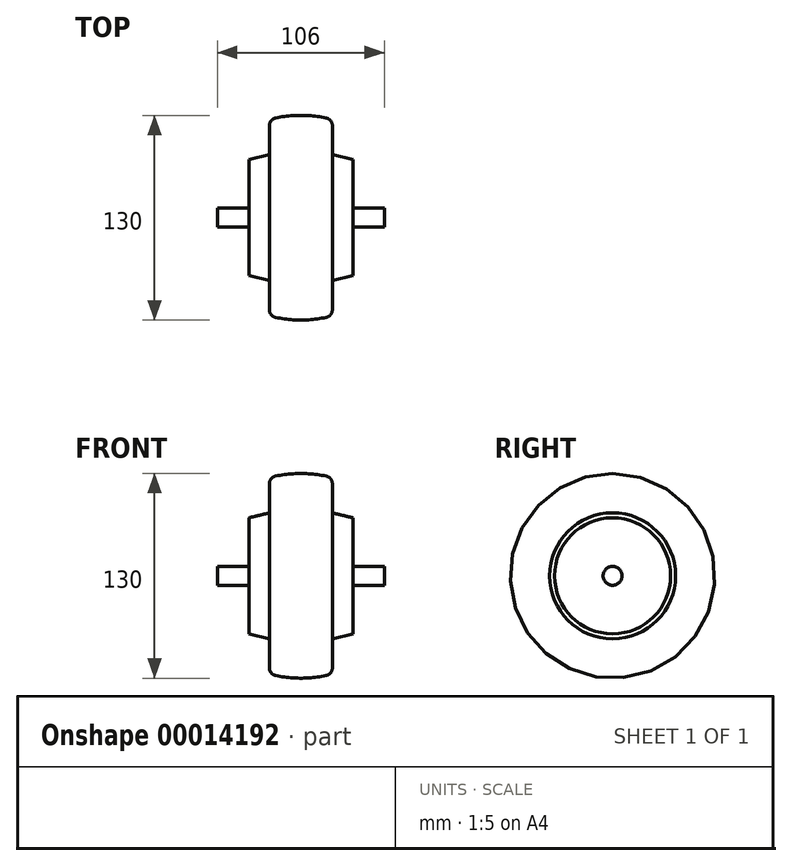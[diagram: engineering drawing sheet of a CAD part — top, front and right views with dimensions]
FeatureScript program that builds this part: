
annotation { "Feature Type Name" : "Feature", "Feature Type Description" : "" }
export const myFeature = defineFeature(function(context is Context, id is Id, definition is map)
    precondition{}
    {
        {
            var Q0;
            Q0=qCreatedBy(makeId("Top.planeOp"),FACE);
            var sketch = newSketch(context, id + "F0", { "sketchPlane" : qUnion([Q0])});
            skLineSegment(sketch, "E0.left", {"start": v(-23.85, 40) * mm, "end": v(-23.85, 58.45) * mm});
            skLineSegment(sketch, "E0.right", {"start": v(16.15, 40) * mm, "end": v(16.15, 58.45) * mm});
            skLineSegment(sketch, "E1.right", {"start": v(-36.85, 0) * mm, "end": v(-36.85, 36.84) * mm});
            skLineSegment(sketch, "E2.MirrorCS", {"start": v(29.15, 0) * mm, "end": v(29.15, 36.84) * mm});
            skLineSegment(sketch, "E3", {"start": v(-23.85, 40) * mm, "end": v(-36.85, 36.84) * mm});
            skLineSegment(sketch, "E4.MirrorCS", {"start": v(16.15, 40) * mm, "end": v(29.15, 36.84) * mm});
            skPoint(sketch, "E5.MirrorCS.end.orphan", {"position": v(29.15, 0) * mm});
            skArc(sketch, "E6", {"start": v(12.18, 63.34) * mm, "mid": v(-3.85, 65) * mm, "end": v(-19.87, 63.34) * mm});
            skArc(sketch, "E7.filletArc", {"start": v(-19.87, 63.34) * mm, "mid": v(-22.73, 61.6) * mm, "end": v(-23.85, 58.45) * mm});
            skArc(sketch, "E8.filletArc", {"start": v(16.15, 58.45) * mm, "mid": v(15.03, 61.6) * mm, "end": v(12.18, 63.34) * mm});
            skLineSegment(sketch, "E9", {"start": v(-36.85, 0) * mm, "end": v(29.15, 0) * mm});
            skSolve(sketch);
        }
        {
            var Q0;
            Q0=qSketchRegion(id+"F0",true);
            var Q1;
            Q1=sQuery(id+"F0.wireOp",EDGE,"E9");
            revolve(context, id + "F1", {"entities" : qUnion([Q0]), "axis" : qUnion([Q1]), "revolveType" : RevolveType.FULL});
        }
        {
            var Q0;
            Q0=makeQuery(id+"F1.opRevolve","SWEPT_FACE",FACE,{"disambiguationData":[OSD([sQuery(id+"F0.wireOp",EDGE,"E2.MirrorCS")])]});
            var sketch = newSketch(context, id + "F2", { "sketchPlane" : qUnion([Q0])});
            skCircle(sketch, "E10", {"center": v(0, 0) * mm, "radius": 6 * mm});
            skSolve(sketch);
        }
        {
            var Q0;
            Q0=qSketchRegion(id+"F2",true);
            extrude(context, id + "F3", {"entities" : qUnion([Q0]), "operationType" : NewBodyOperationType.ADD, "depth" : 20 * mm, "hasSecondDirection" : true, "secondDirectionOppositeDirection" : true, "secondDirectionDepth" : 86 * mm});
        }
    });
